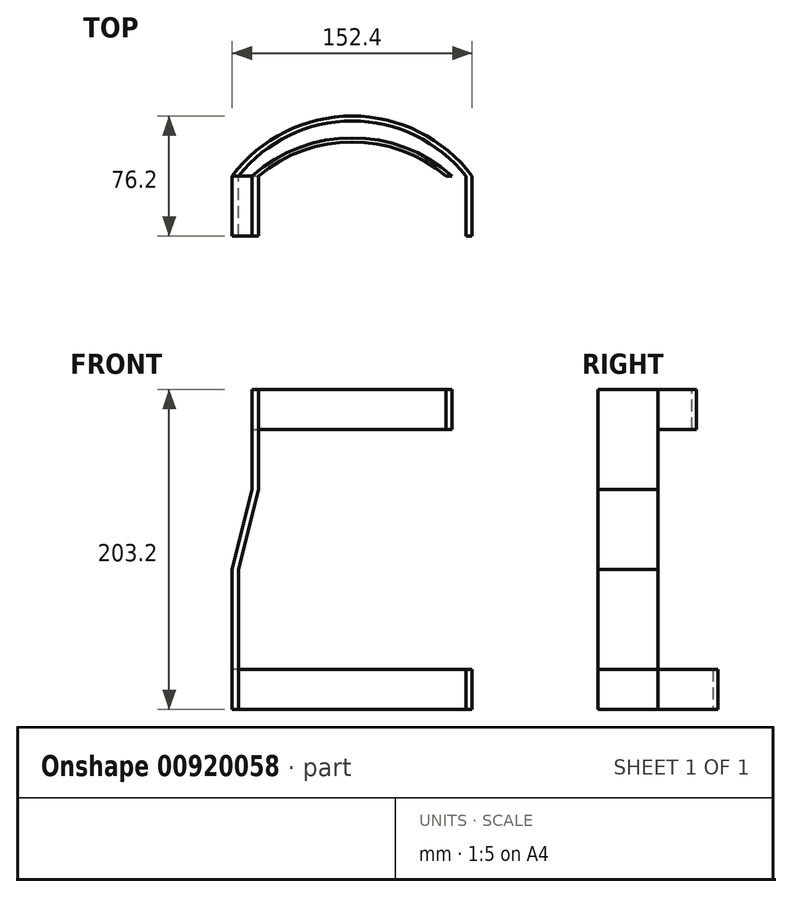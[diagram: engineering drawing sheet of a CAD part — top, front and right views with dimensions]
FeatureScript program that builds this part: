
annotation { "Feature Type Name" : "Feature", "Feature Type Description" : "" }
export const myFeature = defineFeature(function(context is Context, id is Id, definition is map)
    precondition{}
    {
        {
            var Q0;
            Q0=qCreatedBy(makeId("Top.planeOp"),FACE);
            var sketch = newSketch(context, id + "F0", { "sketchPlane" : qUnion([Q0])});
            skArc(sketch, "E0", {"start": v(152.4, 0) * mm, "mid": v(76.2, 38.1) * mm, "end": v(0, 0) * mm});
            skPoint(sketch, "E1", {"position": v(76.2, 38.1) * mm});
            skArc(sketch, "E2.0", {"start": v(148.4, 0) * mm, "mid": v(76.2, 34.93) * mm, "end": v(4, 0) * mm});
            skLineSegment(sketch, "E3", {"start": v(0, 0) * mm, "end": v(4, 0) * mm});
            skLineSegment(sketch, "E4", {"start": v(152.4, 0) * mm, "end": v(148.4, 0) * mm});
            skSolve(sketch);
        }
        {
            var Q0;
            Q0=makeQuery(id+"F0.imprint","IMPRINT",FACE,{"disambiguationData":[TD([[makeQuery(id+"F0.imprint","IMPRINT",EDGE,{"derivedFrom":sQuery(id+"F0.wireOp",EDGE,"E0")}),1.0]])]});
            extrude(context, id + "F1", {"entities" : qUnion([Q0]), "depth" : 25.4 * mm, "offsetDistance" : 25.4 * mm});
        }
        {
            var Q0;
            Q0=makeQuery(id+"F1.opExtrude","SWEPT_FACE",FACE,{"disambiguationData":[OSD([sQuery(id+"F0.wireOp",EDGE,"E4")])]});
            var Q1;
            Q1=makeQuery(id+"F1.opExtrude","SWEPT_FACE",FACE,{"disambiguationData":[OSD([sQuery(id+"F0.wireOp",EDGE,"E3")])]});
            extrude(context, id + "F2", {"entities" : qUnion([Q0, Q1]), "operationType" : NewBodyOperationType.ADD, "depth" : 38.1 * mm, "offsetDistance" : 25.4 * mm});
        }
        {
            var Q0;
            Q0=qCreatedBy(makeId("Front.planeOp"),FACE);
            var sketch = newSketch(context, id + "F3", { "sketchPlane" : qUnion([Q0])});
            skPoint(sketch, "E5.0", {"position": v(4, 25.4) * mm});
            skPoint(sketch, "E6.0", {"position": v(0, 25.4) * mm});
            skLineSegment(sketch, "E7", {"start": v(4, 25.4) * mm, "end": v(0, 25.4) * mm});
            skLineSegment(sketch, "E8", {"start": v(0, 25.4) * mm, "end": v(0, 88.9) * mm});
            skLineSegment(sketch, "E9", {"start": v(0, 88.9) * mm, "end": v(12.7, 139.7) * mm});
            skLineSegment(sketch, "E10", {"start": v(12.7, 139.7) * mm, "end": v(12.7, 203.2) * mm});
            skLineSegment(sketch, "E11", {"start": v(12.7, 203.2) * mm, "end": v(16.7, 203.2) * mm});
            skLineSegment(sketch, "E12", {"start": v(16.7, 203.2) * mm, "end": v(16.7, 139.7) * mm});
            skLineSegment(sketch, "E13", {"start": v(16.7, 139.7) * mm, "end": v(4, 88.9) * mm});
            skLineSegment(sketch, "E14", {"start": v(4, 88.9) * mm, "end": v(4, 25.4) * mm});
            skSolve(sketch);
        }
        {
            var Q0;
            Q0=makeQuery(id+"F3.imprint","IMPRINT",FACE,{"disambiguationData":[TD([[makeQuery(id+"F3.imprint","IMPRINT",EDGE,{"derivedFrom":sQuery(id+"F3.wireOp",EDGE,"E7")}),-1.0]])]});
            extrude(context, id + "F4", {"entities" : qUnion([Q0]), "operationType" : NewBodyOperationType.ADD, "depth" : 38.1 * mm, "offsetDistance" : 25.4 * mm});
        }
        {
            var Q0;
            Q0=qCreatedBy(makeId("Right.planeOp"),FACE);
            cPlane(context, id + "F5", {"entities" : qUnion([Q0]), "cplaneType" : CPlaneType.OFFSET, "offset" : 76.2 * mm, "width" : 152.4 * mm, "height" : 152.4 * mm});
        }
        {
            var Q0;
            Q0=makeQuery(id+"F4.opExtrude","SWEPT_FACE",FACE,{"disambiguationData":[OSD([sQuery(id+"F3.wireOp",EDGE,"E11")])]});
            var sketch = newSketch(context, id + "F6", { "sketchPlane" : qUnion([Q0])});
            skArc(sketch, "E15", {"start": v(135.7, 0) * mm, "mid": v(76.2, 21.63) * mm, "end": v(16.7, 0) * mm});
            skPoint(sketch, "E16.0", {"position": v(139.7, 0) * mm});
            skPoint(sketch, "E17.0", {"position": v(12.7, 0) * mm});
            skPoint(sketch, "E18.0", {"position": v(135.7, 0) * mm});
            skArc(sketch, "E19", {"start": v(139.7, 0) * mm, "mid": v(76.2, 24.25) * mm, "end": v(12.7, 0) * mm});
            skLineSegment(sketch, "E20", {"start": v(12.7, 0) * mm, "end": v(16.7, 0) * mm});
            skLineSegment(sketch, "E21", {"start": v(135.7, 0) * mm, "end": v(139.7, 0) * mm});
            skSolve(sketch);
        }
        {
            var Q0;
            Q0=makeQuery(id+"F6.imprint","IMPRINT",FACE,{"disambiguationData":[TD([[makeQuery(id+"F6.imprint","IMPRINT",EDGE,{"derivedFrom":sQuery(id+"F6.wireOp",EDGE,"E15")}),-1.0]])]});
            extrude(context, id + "F7", {"entities" : qUnion([Q0]), "operationType" : NewBodyOperationType.ADD, "oppositeDirection" : true, "depth" : 25.4 * mm, "offsetDistance" : 25.4 * mm});
        }
    });
